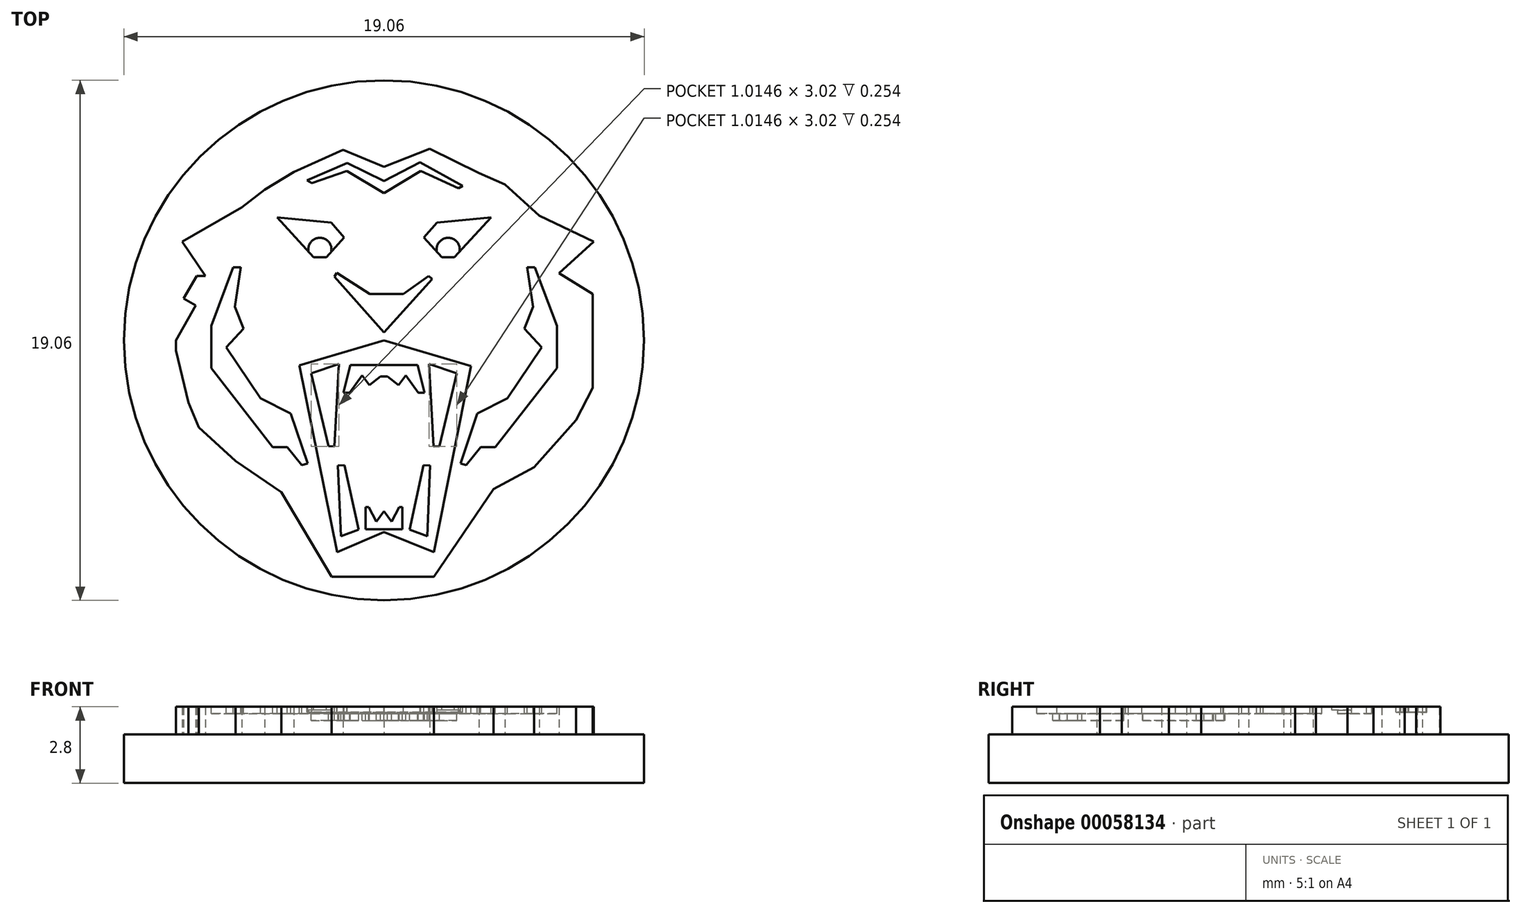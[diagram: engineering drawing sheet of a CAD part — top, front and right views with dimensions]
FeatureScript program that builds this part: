
annotation { "Feature Type Name" : "Feature", "Feature Type Description" : "" }
export const myFeature = defineFeature(function(context is Context, id is Id, definition is map)
    precondition{}
    {
        {
            var Q0;
            Q0=qCreatedBy(makeId("Top.planeOp"),FACE);
            var sketch = newSketch(context, id + "F0", { "sketchPlane" : qUnion([Q0])});
            skCircle(sketch, "E0", {"center": v(0, 0) * mm, "radius": 9.53 * mm});
            skSolve(sketch);
        }
        {
            var Q0;
            Q0=qCreatedBy(makeId("Top.planeOp"),FACE);
            var sketch = newSketch(context, id + "F1", { "sketchPlane" : qUnion([Q0])});
            skLineSegment(sketch, "E1", {"start": v(-7.39, 3.6) * mm, "end": v(-5.2, 4.87) * mm});
            skLineSegment(sketch, "E2", {"start": v(-5.2, 4.87) * mm, "end": v(-4.37, 5.52) * mm});
            skLineSegment(sketch, "E3", {"start": v(-4.37, 5.52) * mm, "end": v(-3.3, 6.17) * mm});
            skLineSegment(sketch, "E4", {"start": v(-3.3, 6.17) * mm, "end": v(-1.5, 6.98) * mm});
            skLineSegment(sketch, "E5", {"start": v(-1.5, 6.98) * mm, "end": v(0, 6.36) * mm});
            skLineSegment(sketch, "E6", {"start": v(0, 6.36) * mm, "end": v(1.67, 7.01) * mm});
            skLineSegment(sketch, "E7", {"start": v(1.67, 7.01) * mm, "end": v(3.47, 6.13) * mm});
            skLineSegment(sketch, "E8", {"start": v(3.47, 6.13) * mm, "end": v(4.43, 5.71) * mm});
            skLineSegment(sketch, "E9", {"start": v(4.43, 5.71) * mm, "end": v(5.69, 4.57) * mm});
            skLineSegment(sketch, "E10", {"start": v(5.69, 4.57) * mm, "end": v(7.68, 3.6) * mm});
            skLineSegment(sketch, "E11", {"start": v(7.68, 3.6) * mm, "end": v(6.42, 2.46) * mm});
            skLineSegment(sketch, "E12", {"start": v(6.42, 2.46) * mm, "end": v(7.64, 1.7) * mm});
            skLineSegment(sketch, "E13", {"start": v(7.64, 1.7) * mm, "end": v(7.64, 1.05) * mm});
            skLineSegment(sketch, "E14", {"start": v(7.64, 1.05) * mm, "end": v(7.64, 0.4) * mm});
            skLineSegment(sketch, "E15", {"start": v(7.64, 0.4) * mm, "end": v(7.64, -0.71) * mm});
            skLineSegment(sketch, "E16", {"start": v(7.64, -0.71) * mm, "end": v(7.64, -1.74) * mm});
            skLineSegment(sketch, "E17", {"start": v(7.64, -1.74) * mm, "end": v(7.03, -2.93) * mm});
            skLineSegment(sketch, "E18", {"start": v(7.03, -2.93) * mm, "end": v(5.5, -4.65) * mm});
            skLineSegment(sketch, "E19", {"start": v(5.5, -4.65) * mm, "end": v(4, -5.45) * mm});
            skLineSegment(sketch, "E20", {"start": v(4, -5.45) * mm, "end": v(1.83, -8.67) * mm});
            skLineSegment(sketch, "E21", {"start": v(1.83, -8.67) * mm, "end": v(-1.92, -8.67) * mm});
            skLineSegment(sketch, "E22", {"start": v(-1.92, -8.67) * mm, "end": v(-3.76, -5.57) * mm});
            skLineSegment(sketch, "E23", {"start": v(-3.76, -5.57) * mm, "end": v(-5.44, -4.42) * mm});
            skLineSegment(sketch, "E24", {"start": v(-5.44, -4.42) * mm, "end": v(-6.78, -3.2) * mm});
            skLineSegment(sketch, "E25", {"start": v(-6.78, -3.2) * mm, "end": v(-7.16, -2.28) * mm});
            skLineSegment(sketch, "E26", {"start": v(-7.16, -2.28) * mm, "end": v(-7.62, -0.37) * mm});
            skLineSegment(sketch, "E27", {"start": v(-7.62, -0.37) * mm, "end": v(-7.62, 0) * mm});
            skLineSegment(sketch, "E28", {"start": v(-7.62, 0) * mm, "end": v(-6.9, 1.28) * mm});
            skLineSegment(sketch, "E29", {"start": v(-6.9, 1.28) * mm, "end": v(-7.34, 1.53) * mm});
            skLineSegment(sketch, "E30", {"start": v(-7.34, 1.53) * mm, "end": v(-6.87, 2.36) * mm});
            skLineSegment(sketch, "E31", {"start": v(-6.87, 2.36) * mm, "end": v(-6.55, 2.36) * mm});
            skLineSegment(sketch, "E32", {"start": v(-6.55, 2.36) * mm, "end": v(-7.39, 3.6) * mm});
            skSolve(sketch);
        }
        {
            var Q0;
            Q0 = qSketchRegion(id + "F1", true);
            extrude(context, id + "F2", {"entities" : qUnion([Q0]), "depth" : 1.02 * mm});
        }
        {
            var Q0;
            Q0 = qSketchRegion(id + "F0", true);
            extrude(context, id + "F3", {"entities" : qUnion([Q0]), "operationType" : NewBodyOperationType.ADD, "oppositeDirection" : true, "depth" : 1.78 * mm});
        }
        {
            var Q0;
            Q0=makeQuery(id+"F2.opExtrude","CAP_FACE",FACE,{"disambiguationData":[OSD([sQuery(id+"F1.wireOp",EDGE,"E1"),sQuery(id+"F1.wireOp",EDGE,"E2"),sQuery(id+"F1.wireOp",EDGE,"E3"),sQuery(id+"F1.wireOp",EDGE,"E4"),sQuery(id+"F1.wireOp",EDGE,"E5"),sQuery(id+"F1.wireOp",EDGE,"E6"),sQuery(id+"F1.wireOp",EDGE,"E7"),sQuery(id+"F1.wireOp",EDGE,"E8"),sQuery(id+"F1.wireOp",EDGE,"E9"),sQuery(id+"F1.wireOp",EDGE,"E10"),sQuery(id+"F1.wireOp",EDGE,"E11"),sQuery(id+"F1.wireOp",EDGE,"E12"),sQuery(id+"F1.wireOp",EDGE,"E13"),sQuery(id+"F1.wireOp",EDGE,"E14"),sQuery(id+"F1.wireOp",EDGE,"E15"),sQuery(id+"F1.wireOp",EDGE,"E16"),sQuery(id+"F1.wireOp",EDGE,"E17"),sQuery(id+"F1.wireOp",EDGE,"E18"),sQuery(id+"F1.wireOp",EDGE,"E19"),sQuery(id+"F1.wireOp",EDGE,"E20"),sQuery(id+"F1.wireOp",EDGE,"E21"),sQuery(id+"F1.wireOp",EDGE,"E22"),sQuery(id+"F1.wireOp",EDGE,"E23"),sQuery(id+"F1.wireOp",EDGE,"E24"),sQuery(id+"F1.wireOp",EDGE,"E25"),sQuery(id+"F1.wireOp",EDGE,"E26"),sQuery(id+"F1.wireOp",EDGE,"E27"),sQuery(id+"F1.wireOp",EDGE,"E28"),sQuery(id+"F1.wireOp",EDGE,"E29"),sQuery(id+"F1.wireOp",EDGE,"E30"),sQuery(id+"F1.wireOp",EDGE,"E31"),sQuery(id+"F1.wireOp",EDGE,"E32")])],"isStart":false});
            var sketch = newSketch(context, id + "F4", { "sketchPlane" : qUnion([Q0])});
            skLineSegment(sketch, "E33", {"start": v(15.35, 3.18) * mm, "end": v(17.71, 4.55) * mm});
            skLineSegment(sketch, "E34", {"start": v(17.71, 4.55) * mm, "end": v(18.63, 5.25) * mm});
            skLineSegment(sketch, "E35", {"start": v(18.63, 5.25) * mm, "end": v(19.79, 5.96) * mm});
            skLineSegment(sketch, "E36", {"start": v(19.79, 5.96) * mm, "end": v(21.74, 6.83) * mm});
            skLineSegment(sketch, "E37", {"start": v(21.74, 6.83) * mm, "end": v(23.36, 6.16) * mm});
            skLineSegment(sketch, "E38", {"start": v(23.36, 6.16) * mm, "end": v(25.18, 6.87) * mm});
            skLineSegment(sketch, "E39", {"start": v(25.18, 6.87) * mm, "end": v(27.13, 5.91) * mm});
            skLineSegment(sketch, "E40", {"start": v(27.13, 5.91) * mm, "end": v(28.16, 5.46) * mm});
            skLineSegment(sketch, "E41", {"start": v(28.16, 5.46) * mm, "end": v(29.53, 4.21) * mm});
            skLineSegment(sketch, "E42", {"start": v(29.53, 4.21) * mm, "end": v(31.69, 3.18) * mm});
            skLineSegment(sketch, "E43", {"start": v(31.69, 3.18) * mm, "end": v(30.32, 1.93) * mm});
            skLineSegment(sketch, "E44", {"start": v(30.32, 1.93) * mm, "end": v(31.65, 1.1) * mm});
            skLineSegment(sketch, "E45", {"start": v(31.65, 1.1) * mm, "end": v(31.65, 0.4) * mm});
            skLineSegment(sketch, "E46", {"start": v(31.65, 0.4) * mm, "end": v(31.65, -0.3) * mm});
            skLineSegment(sketch, "E47", {"start": v(31.65, -0.3) * mm, "end": v(31.65, -1.5) * mm});
            skLineSegment(sketch, "E48", {"start": v(31.65, -1.5) * mm, "end": v(31.65, -2.63) * mm});
            skLineSegment(sketch, "E49", {"start": v(31.65, -2.63) * mm, "end": v(30.98, -3.91) * mm});
            skLineSegment(sketch, "E50", {"start": v(30.98, -3.91) * mm, "end": v(29.32, -5.78) * mm});
            skLineSegment(sketch, "E51", {"start": v(29.32, -5.78) * mm, "end": v(27.7, -6.65) * mm});
            skLineSegment(sketch, "E52", {"start": v(27.7, -6.65) * mm, "end": v(25.34, -10.13) * mm});
            skLineSegment(sketch, "E53", {"start": v(25.34, -10.13) * mm, "end": v(21.28, -10.13) * mm});
            skLineSegment(sketch, "E54", {"start": v(21.28, -10.13) * mm, "end": v(19.29, -6.77) * mm});
            skLineSegment(sketch, "E55", {"start": v(19.29, -6.77) * mm, "end": v(17.46, -5.53) * mm});
            skLineSegment(sketch, "E56", {"start": v(17.46, -5.53) * mm, "end": v(16.01, -4.2) * mm});
            skLineSegment(sketch, "E57", {"start": v(16.01, -4.2) * mm, "end": v(15.6, -3.2) * mm});
            skLineSegment(sketch, "E58", {"start": v(15.6, -3.2) * mm, "end": v(15.1, -1.13) * mm});
            skLineSegment(sketch, "E59", {"start": v(15.1, -1.13) * mm, "end": v(15.1, -0.74) * mm});
            skLineSegment(sketch, "E60", {"start": v(15.1, -0.74) * mm, "end": v(15.89, 0.65) * mm});
            skLineSegment(sketch, "E61", {"start": v(15.89, 0.65) * mm, "end": v(15.4, 0.92) * mm});
            skLineSegment(sketch, "E62", {"start": v(15.4, 0.92) * mm, "end": v(15.92, 1.82) * mm});
            skLineSegment(sketch, "E63", {"start": v(15.92, 1.82) * mm, "end": v(16.26, 1.82) * mm});
            skLineSegment(sketch, "E64", {"start": v(16.26, 1.82) * mm, "end": v(15.35, 3.18) * mm});
            skLineSegment(sketch, "E65", {"start": v(18.44, 1.72) * mm, "end": v(19.91, 2.58) * mm});
            skLineSegment(sketch, "E66", {"start": v(19.91, 2.58) * mm, "end": v(20.48, 3.02) * mm});
            skLineSegment(sketch, "E67", {"start": v(20.48, 3.02) * mm, "end": v(21.2, 3.46) * mm});
            skLineSegment(sketch, "E68", {"start": v(21.2, 3.46) * mm, "end": v(22.43, 4) * mm});
            skLineSegment(sketch, "E69", {"start": v(22.43, 4) * mm, "end": v(23.44, 3.59) * mm});
            skLineSegment(sketch, "E70", {"start": v(23.44, 3.59) * mm, "end": v(24.58, 4.03) * mm});
            skLineSegment(sketch, "E71", {"start": v(24.58, 4.03) * mm, "end": v(25.8, 3.43) * mm});
            skLineSegment(sketch, "E72", {"start": v(25.8, 3.43) * mm, "end": v(26.44, 3.15) * mm});
            skLineSegment(sketch, "E73", {"start": v(26.44, 3.15) * mm, "end": v(27.3, 2.37) * mm});
            skLineSegment(sketch, "E74", {"start": v(27.3, 2.37) * mm, "end": v(28.65, 1.72) * mm});
            skLineSegment(sketch, "E75", {"start": v(28.65, 1.72) * mm, "end": v(27.8, 0.94) * mm});
            skLineSegment(sketch, "E76", {"start": v(27.8, 0.94) * mm, "end": v(28.62, 0.43) * mm});
            skLineSegment(sketch, "E77", {"start": v(28.62, 0.43) * mm, "end": v(28.62, -0.66) * mm});
            skLineSegment(sketch, "E78", {"start": v(28.62, -0.66) * mm, "end": v(28.62, -1.1) * mm});
            skLineSegment(sketch, "E79", {"start": v(28.62, -1.1) * mm, "end": v(28.62, -1.86) * mm});
            skLineSegment(sketch, "E80", {"start": v(28.62, -1.86) * mm, "end": v(28.62, -1.9) * mm});
            skLineSegment(sketch, "E81", {"start": v(28.62, -1.9) * mm, "end": v(28.2, -2.71) * mm});
            skLineSegment(sketch, "E82", {"start": v(28.2, -2.71) * mm, "end": v(27.17, -3.88) * mm});
            skLineSegment(sketch, "E83", {"start": v(27.17, -3.88) * mm, "end": v(26.16, -4.42) * mm});
            skLineSegment(sketch, "E84", {"start": v(26.16, -4.42) * mm, "end": v(24.68, -6.6) * mm});
            skLineSegment(sketch, "E85", {"start": v(24.68, -6.6) * mm, "end": v(22.14, -6.6) * mm});
            skLineSegment(sketch, "E86", {"start": v(22.14, -6.6) * mm, "end": v(20.9, -4.5) * mm});
            skLineSegment(sketch, "E87", {"start": v(20.9, -4.5) * mm, "end": v(19.76, -3.72) * mm});
            skLineSegment(sketch, "E88", {"start": v(19.76, -3.72) * mm, "end": v(18.85, -2.9) * mm});
            skLineSegment(sketch, "E89", {"start": v(18.85, -2.9) * mm, "end": v(18.6, -2.27) * mm});
            skLineSegment(sketch, "E90", {"start": v(18.6, -2.27) * mm, "end": v(18.28, -0.97) * mm});
            skLineSegment(sketch, "E91", {"start": v(18.28, -0.97) * mm, "end": v(18.28, -0.72) * mm});
            skLineSegment(sketch, "E92", {"start": v(18.28, -0.72) * mm, "end": v(18.77, 0.14) * mm});
            skLineSegment(sketch, "E93", {"start": v(18.77, 0.14) * mm, "end": v(18.47, 0.31) * mm});
            skLineSegment(sketch, "E94", {"start": v(18.47, 0.31) * mm, "end": v(18.8, 0.87) * mm});
            skLineSegment(sketch, "E95", {"start": v(18.8, 0.87) * mm, "end": v(19, 0.87) * mm});
            skLineSegment(sketch, "E96", {"start": v(19, 0.87) * mm, "end": v(18.44, 1.72) * mm});
            skLineSegment(sketch, "E97", {"start": v(18.44, 1.71) * mm, "end": v(19.91, 2.57) * mm});
            skLineSegment(sketch, "E98", {"start": v(19.91, 2.57) * mm, "end": v(20.48, 3.01) * mm});
            skLineSegment(sketch, "E99", {"start": v(20.48, 3.01) * mm, "end": v(21.2, 3.45) * mm});
            skLineSegment(sketch, "E100", {"start": v(21.2, 3.45) * mm, "end": v(22.43, 4) * mm});
            skLineSegment(sketch, "E101", {"start": v(22.43, 4) * mm, "end": v(23.44, 3.58) * mm});
            skLineSegment(sketch, "E102", {"start": v(23.44, 3.58) * mm, "end": v(25.3, 4.85) * mm});
            skLineSegment(sketch, "E103", {"start": v(25.3, 4.85) * mm, "end": v(25.8, 3.43) * mm});
            skLineSegment(sketch, "E104", {"start": v(25.8, 3.43) * mm, "end": v(26.44, 3.14) * mm});
            skLineSegment(sketch, "E105", {"start": v(26.44, 3.14) * mm, "end": v(27.3, 2.36) * mm});
            skLineSegment(sketch, "E106", {"start": v(27.3, 2.36) * mm, "end": v(28.65, 1.71) * mm});
            skLineSegment(sketch, "E107", {"start": v(28.65, 1.71) * mm, "end": v(27.8, 0.94) * mm});
            skLineSegment(sketch, "E108", {"start": v(27.8, 0.94) * mm, "end": v(28.62, 0.42) * mm});
            skLineSegment(sketch, "E109", {"start": v(28.62, 0.42) * mm, "end": v(28.62, -0.6) * mm});
            skLineSegment(sketch, "E110", {"start": v(28.62, -0.6) * mm, "end": v(28.62, -1.04) * mm});
            skLineSegment(sketch, "E111", {"start": v(28.62, -1.04) * mm, "end": v(28.62, -1.79) * mm});
            skLineSegment(sketch, "E112", {"start": v(28.62, -1.79) * mm, "end": v(28.62, -1.91) * mm});
            skLineSegment(sketch, "E113", {"start": v(28.62, -1.91) * mm, "end": v(28.2, -2.72) * mm});
            skLineSegment(sketch, "E114", {"start": v(28.2, -2.72) * mm, "end": v(27.17, -3.88) * mm});
            skLineSegment(sketch, "E115", {"start": v(27.17, -3.88) * mm, "end": v(26.16, -4.43) * mm});
            skLineSegment(sketch, "E116", {"start": v(26.16, -4.43) * mm, "end": v(24.68, -6.6) * mm});
            skLineSegment(sketch, "E117", {"start": v(20.9, -4.5) * mm, "end": v(19.76, -3.73) * mm});
            skLineSegment(sketch, "E118", {"start": v(19.76, -3.73) * mm, "end": v(18.85, -2.9) * mm});
            skLineSegment(sketch, "E119", {"start": v(18.85, -2.9) * mm, "end": v(18.6, -2.28) * mm});
            skLineSegment(sketch, "E120", {"start": v(18.6, -2.28) * mm, "end": v(18.28, -0.98) * mm});
            skLineSegment(sketch, "E121", {"start": v(18.28, -0.98) * mm, "end": v(18.28, -0.73) * mm});
            skLineSegment(sketch, "E122", {"start": v(18.28, -0.73) * mm, "end": v(18.77, 0.13) * mm});
            skLineSegment(sketch, "E123", {"start": v(18.77, 0.13) * mm, "end": v(18.47, 0.3) * mm});
            skLineSegment(sketch, "E124", {"start": v(18.47, 0.3) * mm, "end": v(18.8, 0.87) * mm});
            skLineSegment(sketch, "E125", {"start": v(19, 0.87) * mm, "end": v(18.44, 1.71) * mm});
            skSolve(sketch);
        }
        {
            var Q0;
            Q0=makeQuery(id+"F4.imprint","IMPRINT",FACE,{"disambiguationData":[TD([[makeQuery(id+"F4.imprint","IMPRINT",EDGE,{"derivedFrom":sQuery(id+"F4.wireOp",EDGE,"E33")}),-1.0]])]});
            extrude(context, id + "F5", {"entities" : qUnion([Q0]), "depth" : 0.74 * mm});
        }
        {
            var Q0;
            Q0=makeQuery(id+"F5.opExtrude","SWEPT_BODY",BODY,{"disambiguationData":[OSD([sQuery(id+"F4.wireOp",EDGE,"E33"),sQuery(id+"F4.wireOp",EDGE,"E34"),sQuery(id+"F4.wireOp",EDGE,"E35"),sQuery(id+"F4.wireOp",EDGE,"E36"),sQuery(id+"F4.wireOp",EDGE,"E37"),sQuery(id+"F4.wireOp",EDGE,"E38"),sQuery(id+"F4.wireOp",EDGE,"E39"),sQuery(id+"F4.wireOp",EDGE,"E40"),sQuery(id+"F4.wireOp",EDGE,"E41"),sQuery(id+"F4.wireOp",EDGE,"E42"),sQuery(id+"F4.wireOp",EDGE,"E43"),sQuery(id+"F4.wireOp",EDGE,"E44"),sQuery(id+"F4.wireOp",EDGE,"E45"),sQuery(id+"F4.wireOp",EDGE,"E46"),sQuery(id+"F4.wireOp",EDGE,"E47"),sQuery(id+"F4.wireOp",EDGE,"E48"),sQuery(id+"F4.wireOp",EDGE,"E49"),sQuery(id+"F4.wireOp",EDGE,"E50"),sQuery(id+"F4.wireOp",EDGE,"E51"),sQuery(id+"F4.wireOp",EDGE,"E52"),sQuery(id+"F4.wireOp",EDGE,"E53"),sQuery(id+"F4.wireOp",EDGE,"E54"),sQuery(id+"F4.wireOp",EDGE,"E55"),sQuery(id+"F4.wireOp",EDGE,"E56"),sQuery(id+"F4.wireOp",EDGE,"E57"),sQuery(id+"F4.wireOp",EDGE,"E58"),sQuery(id+"F4.wireOp",EDGE,"E59"),sQuery(id+"F4.wireOp",EDGE,"E60"),sQuery(id+"F4.wireOp",EDGE,"E61"),sQuery(id+"F4.wireOp",EDGE,"E62"),sQuery(id+"F4.wireOp",EDGE,"E63"),sQuery(id+"F4.wireOp",EDGE,"E64"),sQuery(id+"F4.wireOp",EDGE,"E65"),sQuery(id+"F4.wireOp",EDGE,"E66"),sQuery(id+"F4.wireOp",EDGE,"E67"),sQuery(id+"F4.wireOp",EDGE,"E68"),sQuery(id+"F4.wireOp",EDGE,"E69"),sQuery(id+"F4.wireOp",EDGE,"E70"),sQuery(id+"F4.wireOp",EDGE,"E71"),sQuery(id+"F4.wireOp",EDGE,"E72"),sQuery(id+"F4.wireOp",EDGE,"E73"),sQuery(id+"F4.wireOp",EDGE,"E74"),sQuery(id+"F4.wireOp",EDGE,"E75"),sQuery(id+"F4.wireOp",EDGE,"E76"),sQuery(id+"F4.wireOp",EDGE,"E77"),sQuery(id+"F4.wireOp",EDGE,"E91"),sQuery(id+"F4.wireOp",EDGE,"E92"),sQuery(id+"F4.wireOp",EDGE,"E93"),sQuery(id+"F4.wireOp",EDGE,"E94"),sQuery(id+"F4.wireOp",EDGE,"E95"),sQuery(id+"F4.wireOp",EDGE,"E96"),sQuery(id+"F4.wireOp",EDGE,"E97"),sQuery(id+"F4.wireOp",EDGE,"E102"),sQuery(id+"F4.wireOp",EDGE,"E103"),sQuery(id+"F4.wireOp",EDGE,"E106"),sQuery(id+"F4.wireOp",EDGE,"E107"),sQuery(id+"F4.wireOp",EDGE,"E109"),sQuery(id+"F4.wireOp",EDGE,"E110"),sQuery(id+"F4.wireOp",EDGE,"E111"),sQuery(id+"F4.wireOp",EDGE,"E112"),sQuery(id+"F4.wireOp",EDGE,"E113"),sQuery(id+"F4.wireOp",EDGE,"E114"),sQuery(id+"F4.wireOp",EDGE,"E115"),sQuery(id+"F4.wireOp",EDGE,"E116"),sQuery(id+"F4.wireOp",EDGE,"E85"),sQuery(id+"F4.wireOp",EDGE,"E86"),sQuery(id+"F4.wireOp",EDGE,"E117"),sQuery(id+"F4.wireOp",EDGE,"E118"),sQuery(id+"F4.wireOp",EDGE,"E119"),sQuery(id+"F4.wireOp",EDGE,"E120"),sQuery(id+"F4.wireOp",EDGE,"E121"),sQuery(id+"F4.wireOp",EDGE,"E123"),sQuery(id+"F4.wireOp",EDGE,"E124"),sQuery(id+"F4.wireOp",EDGE,"E125")])]});
            deleteBodies(context, id + "F6", {"entities" : qUnion([Q0])});
        }
        {
            var Q0;
            Q0=makeQuery(id+"F2.opExtrude","CAP_FACE",FACE,{"disambiguationData":[OSD([sQuery(id+"F1.wireOp",EDGE,"E1"),sQuery(id+"F1.wireOp",EDGE,"E2"),sQuery(id+"F1.wireOp",EDGE,"E3"),sQuery(id+"F1.wireOp",EDGE,"E4"),sQuery(id+"F1.wireOp",EDGE,"E5"),sQuery(id+"F1.wireOp",EDGE,"E6"),sQuery(id+"F1.wireOp",EDGE,"E7"),sQuery(id+"F1.wireOp",EDGE,"E8"),sQuery(id+"F1.wireOp",EDGE,"E9"),sQuery(id+"F1.wireOp",EDGE,"E10"),sQuery(id+"F1.wireOp",EDGE,"E11"),sQuery(id+"F1.wireOp",EDGE,"E12"),sQuery(id+"F1.wireOp",EDGE,"E13"),sQuery(id+"F1.wireOp",EDGE,"E14"),sQuery(id+"F1.wireOp",EDGE,"E15"),sQuery(id+"F1.wireOp",EDGE,"E16"),sQuery(id+"F1.wireOp",EDGE,"E17"),sQuery(id+"F1.wireOp",EDGE,"E18"),sQuery(id+"F1.wireOp",EDGE,"E19"),sQuery(id+"F1.wireOp",EDGE,"E20"),sQuery(id+"F1.wireOp",EDGE,"E21"),sQuery(id+"F1.wireOp",EDGE,"E22"),sQuery(id+"F1.wireOp",EDGE,"E23"),sQuery(id+"F1.wireOp",EDGE,"E24"),sQuery(id+"F1.wireOp",EDGE,"E25"),sQuery(id+"F1.wireOp",EDGE,"E26"),sQuery(id+"F1.wireOp",EDGE,"E27"),sQuery(id+"F1.wireOp",EDGE,"E28"),sQuery(id+"F1.wireOp",EDGE,"E29"),sQuery(id+"F1.wireOp",EDGE,"E30"),sQuery(id+"F1.wireOp",EDGE,"E31"),sQuery(id+"F1.wireOp",EDGE,"E32")])],"isStart":false});
            var sketch = newSketch(context, id + "F7", { "sketchPlane" : qUnion([Q0])});
            skLineSegment(sketch, "E126", {"start": v(-2.82, 5.86) * mm, "end": v(-1.35, 6.5) * mm});
            skLineSegment(sketch, "E127", {"start": v(-1.35, 6.5) * mm, "end": v(0, 5.84) * mm});
            skLineSegment(sketch, "E128", {"start": v(0, 5.84) * mm, "end": v(1.32, 6.52) * mm});
            skLineSegment(sketch, "E129", {"start": v(1.32, 6.52) * mm, "end": v(2.88, 5.67) * mm});
            skLineSegment(sketch, "E130", {"start": v(2.88, 5.67) * mm, "end": v(2.73, 5.57) * mm});
            skLineSegment(sketch, "E131", {"start": v(2.73, 5.57) * mm, "end": v(1.34, 6.2) * mm});
            skLineSegment(sketch, "E132", {"start": v(1.34, 6.2) * mm, "end": v(0, 5.39) * mm});
            skLineSegment(sketch, "E133", {"start": v(0, 5.39) * mm, "end": v(-1.36, 6.2) * mm});
            skLineSegment(sketch, "E134", {"start": v(-1.36, 6.2) * mm, "end": v(-2.64, 5.76) * mm});
            skLineSegment(sketch, "E135", {"start": v(-2.64, 5.76) * mm, "end": v(-2.82, 5.86) * mm});
            skSolve(sketch);
        }
        {
            var Q0;
            Q0 = qSketchRegion(id + "F7", true);
            extrude(context, id + "F8", {"entities" : qUnion([Q0]), "operationType" : NewBodyOperationType.REMOVE, "oppositeDirection" : true, "depth" : 0.2 * mm});
        }
        {
            var Q0;
            Q0=makeQuery(id+"F2.opExtrude","CAP_FACE",FACE,{"disambiguationData":[OSD([sQuery(id+"F1.wireOp",EDGE,"E1"),sQuery(id+"F1.wireOp",EDGE,"E2"),sQuery(id+"F1.wireOp",EDGE,"E3"),sQuery(id+"F1.wireOp",EDGE,"E4"),sQuery(id+"F1.wireOp",EDGE,"E5"),sQuery(id+"F1.wireOp",EDGE,"E6"),sQuery(id+"F1.wireOp",EDGE,"E7"),sQuery(id+"F1.wireOp",EDGE,"E8"),sQuery(id+"F1.wireOp",EDGE,"E9"),sQuery(id+"F1.wireOp",EDGE,"E10"),sQuery(id+"F1.wireOp",EDGE,"E11"),sQuery(id+"F1.wireOp",EDGE,"E12"),sQuery(id+"F1.wireOp",EDGE,"E13"),sQuery(id+"F1.wireOp",EDGE,"E14"),sQuery(id+"F1.wireOp",EDGE,"E15"),sQuery(id+"F1.wireOp",EDGE,"E16"),sQuery(id+"F1.wireOp",EDGE,"E17"),sQuery(id+"F1.wireOp",EDGE,"E18"),sQuery(id+"F1.wireOp",EDGE,"E19"),sQuery(id+"F1.wireOp",EDGE,"E20"),sQuery(id+"F1.wireOp",EDGE,"E21"),sQuery(id+"F1.wireOp",EDGE,"E22"),sQuery(id+"F1.wireOp",EDGE,"E23"),sQuery(id+"F1.wireOp",EDGE,"E24"),sQuery(id+"F1.wireOp",EDGE,"E25"),sQuery(id+"F1.wireOp",EDGE,"E26"),sQuery(id+"F1.wireOp",EDGE,"E27"),sQuery(id+"F1.wireOp",EDGE,"E28"),sQuery(id+"F1.wireOp",EDGE,"E29"),sQuery(id+"F1.wireOp",EDGE,"E30"),sQuery(id+"F1.wireOp",EDGE,"E31"),sQuery(id+"F1.wireOp",EDGE,"E32")])],"isStart":false});
            var sketch = newSketch(context, id + "F9", { "sketchPlane" : qUnion([Q0])});
            skLineSegment(sketch, "E136", {"start": v(-2.8, -4.5) * mm, "end": v(-3.42, -2.68) * mm});
            skLineSegment(sketch, "E137", {"start": v(-3.42, -2.68) * mm, "end": v(-4.52, -2.13) * mm});
            skLineSegment(sketch, "E138", {"start": v(-4.52, -2.13) * mm, "end": v(-5.78, -0.26) * mm});
            skLineSegment(sketch, "E139", {"start": v(-5.78, -0.26) * mm, "end": v(-5.14, 0.43) * mm});
            skLineSegment(sketch, "E140", {"start": v(-5.14, 0.43) * mm, "end": v(-5.46, 1.23) * mm});
            skLineSegment(sketch, "E141", {"start": v(-5.46, 1.23) * mm, "end": v(-5.25, 2.68) * mm});
            skLineSegment(sketch, "E142", {"start": v(-5.25, 2.68) * mm, "end": v(-5.52, 2.68) * mm});
            skLineSegment(sketch, "E143", {"start": v(-5.52, 2.68) * mm, "end": v(-6.33, 0.53) * mm});
            skLineSegment(sketch, "E144", {"start": v(-6.33, 0.53) * mm, "end": v(-6.33, -1.02) * mm});
            skLineSegment(sketch, "E145", {"start": v(-6.33, -1.02) * mm, "end": v(-4.08, -3.91) * mm});
            skLineSegment(sketch, "E146", {"start": v(-4.08, -3.91) * mm, "end": v(-3.55, -3.91) * mm});
            skLineSegment(sketch, "E147", {"start": v(-3.55, -3.91) * mm, "end": v(-3.01, -4.57) * mm});
            skLineSegment(sketch, "E148", {"start": v(-3.01, -4.57) * mm, "end": v(-2.8, -4.5) * mm});
            skLineSegment(sketch, "E149.MirrorCS", {"start": v(5.25, 2.68) * mm, "end": v(5.52, 2.68) * mm});
            skLineSegment(sketch, "E150.MirrorCS", {"start": v(4.08, -3.91) * mm, "end": v(3.55, -3.91) * mm});
            skLineSegment(sketch, "E151.MirrorCS", {"start": v(3.01, -4.57) * mm, "end": v(2.8, -4.5) * mm});
            skLineSegment(sketch, "E152.MirrorCS", {"start": v(2.8, -4.5) * mm, "end": v(3.42, -2.68) * mm});
            skLineSegment(sketch, "E153.MirrorCS", {"start": v(3.42, -2.68) * mm, "end": v(4.52, -2.13) * mm});
            skLineSegment(sketch, "E154.MirrorCS", {"start": v(4.52, -2.13) * mm, "end": v(5.78, -0.26) * mm});
            skLineSegment(sketch, "E155.MirrorCS", {"start": v(5.78, -0.26) * mm, "end": v(5.14, 0.43) * mm});
            skLineSegment(sketch, "E156.MirrorCS", {"start": v(5.14, 0.43) * mm, "end": v(5.46, 1.23) * mm});
            skLineSegment(sketch, "E157.MirrorCS", {"start": v(5.46, 1.23) * mm, "end": v(5.25, 2.68) * mm});
            skLineSegment(sketch, "E158.MirrorCS", {"start": v(5.52, 2.68) * mm, "end": v(6.33, 0.53) * mm});
            skLineSegment(sketch, "E159.MirrorCS", {"start": v(6.33, 0.53) * mm, "end": v(6.33, -1.02) * mm});
            skLineSegment(sketch, "E160.MirrorCS", {"start": v(3.55, -3.91) * mm, "end": v(3.01, -4.57) * mm});
            skLineSegment(sketch, "E161.MirrorCS", {"start": v(6.33, -1.02) * mm, "end": v(4.08, -3.91) * mm});
            skSolve(sketch);
        }
        {
            var Q0;
            Q0 = qSketchRegion(id + "F9", true);
            extrude(context, id + "F10", {"entities" : qUnion([Q0]), "operationType" : NewBodyOperationType.REMOVE, "oppositeDirection" : true, "depth" : 0.25 * mm});
        }
        {
            var Q0;
            Q0=makeQuery(id+"F2.opExtrude","CAP_FACE",FACE,{"disambiguationData":[OSD([sQuery(id+"F1.wireOp",EDGE,"E1"),sQuery(id+"F1.wireOp",EDGE,"E2"),sQuery(id+"F1.wireOp",EDGE,"E3"),sQuery(id+"F1.wireOp",EDGE,"E4"),sQuery(id+"F1.wireOp",EDGE,"E5"),sQuery(id+"F1.wireOp",EDGE,"E6"),sQuery(id+"F1.wireOp",EDGE,"E7"),sQuery(id+"F1.wireOp",EDGE,"E8"),sQuery(id+"F1.wireOp",EDGE,"E9"),sQuery(id+"F1.wireOp",EDGE,"E10"),sQuery(id+"F1.wireOp",EDGE,"E11"),sQuery(id+"F1.wireOp",EDGE,"E12"),sQuery(id+"F1.wireOp",EDGE,"E13"),sQuery(id+"F1.wireOp",EDGE,"E14"),sQuery(id+"F1.wireOp",EDGE,"E15"),sQuery(id+"F1.wireOp",EDGE,"E16"),sQuery(id+"F1.wireOp",EDGE,"E17"),sQuery(id+"F1.wireOp",EDGE,"E18"),sQuery(id+"F1.wireOp",EDGE,"E19"),sQuery(id+"F1.wireOp",EDGE,"E20"),sQuery(id+"F1.wireOp",EDGE,"E21"),sQuery(id+"F1.wireOp",EDGE,"E22"),sQuery(id+"F1.wireOp",EDGE,"E23"),sQuery(id+"F1.wireOp",EDGE,"E24"),sQuery(id+"F1.wireOp",EDGE,"E25"),sQuery(id+"F1.wireOp",EDGE,"E26"),sQuery(id+"F1.wireOp",EDGE,"E27"),sQuery(id+"F1.wireOp",EDGE,"E28"),sQuery(id+"F1.wireOp",EDGE,"E29"),sQuery(id+"F1.wireOp",EDGE,"E30"),sQuery(id+"F1.wireOp",EDGE,"E31"),sQuery(id+"F1.wireOp",EDGE,"E32")])],"isStart":false});
            var sketch = newSketch(context, id + "F11", { "sketchPlane" : qUnion([Q0])});
            skLineSegment(sketch, "E162", {"start": v(-3.1, -0.92) * mm, "end": v(0, 0) * mm});
            skLineSegment(sketch, "E163", {"start": v(0, 0) * mm, "end": v(3.18, -0.94) * mm});
            skLineSegment(sketch, "E164", {"start": v(3.18, -0.94) * mm, "end": v(1.82, -7.77) * mm});
            skLineSegment(sketch, "E165", {"start": v(1.82, -7.77) * mm, "end": v(0, -7.03) * mm});
            skLineSegment(sketch, "E166", {"start": v(0, -7.03) * mm, "end": v(-1.71, -7.77) * mm});
            skLineSegment(sketch, "E167", {"start": v(-1.71, -7.77) * mm, "end": v(-3.1, -0.92) * mm});
            skSolve(sketch);
        }
        {
            var Q0;
            Q0 = qSketchRegion(id + "F11", true);
            extrude(context, id + "F12", {"entities" : qUnion([Q0]), "operationType" : NewBodyOperationType.REMOVE, "oppositeDirection" : true, "depth" : 0.25 * mm});
        }
        {
            var Q0;
            Q0=makeQuery(id+"F2.opExtrude","CAP_FACE",FACE,{"disambiguationData":[OSD([sQuery(id+"F1.wireOp",EDGE,"E1"),sQuery(id+"F1.wireOp",EDGE,"E2"),sQuery(id+"F1.wireOp",EDGE,"E3"),sQuery(id+"F1.wireOp",EDGE,"E4"),sQuery(id+"F1.wireOp",EDGE,"E5"),sQuery(id+"F1.wireOp",EDGE,"E6"),sQuery(id+"F1.wireOp",EDGE,"E7"),sQuery(id+"F1.wireOp",EDGE,"E8"),sQuery(id+"F1.wireOp",EDGE,"E9"),sQuery(id+"F1.wireOp",EDGE,"E10"),sQuery(id+"F1.wireOp",EDGE,"E11"),sQuery(id+"F1.wireOp",EDGE,"E12"),sQuery(id+"F1.wireOp",EDGE,"E13"),sQuery(id+"F1.wireOp",EDGE,"E14"),sQuery(id+"F1.wireOp",EDGE,"E15"),sQuery(id+"F1.wireOp",EDGE,"E16"),sQuery(id+"F1.wireOp",EDGE,"E17"),sQuery(id+"F1.wireOp",EDGE,"E18"),sQuery(id+"F1.wireOp",EDGE,"E19"),sQuery(id+"F1.wireOp",EDGE,"E20"),sQuery(id+"F1.wireOp",EDGE,"E21"),sQuery(id+"F1.wireOp",EDGE,"E22"),sQuery(id+"F1.wireOp",EDGE,"E23"),sQuery(id+"F1.wireOp",EDGE,"E24"),sQuery(id+"F1.wireOp",EDGE,"E25"),sQuery(id+"F1.wireOp",EDGE,"E26"),sQuery(id+"F1.wireOp",EDGE,"E27"),sQuery(id+"F1.wireOp",EDGE,"E28"),sQuery(id+"F1.wireOp",EDGE,"E29"),sQuery(id+"F1.wireOp",EDGE,"E30"),sQuery(id+"F1.wireOp",EDGE,"E31"),sQuery(id+"F1.wireOp",EDGE,"E32")])],"isStart":false});
            var sketch = newSketch(context, id + "F13", { "sketchPlane" : qUnion([Q0])});
            skLineSegment(sketch, "E168", {"start": v(0, 0.29) * mm, "end": v(1.76, 2.24) * mm});
            skLineSegment(sketch, "E169", {"start": v(1.76, 2.24) * mm, "end": v(1.64, 2.36) * mm});
            skLineSegment(sketch, "E170", {"start": v(1.64, 2.36) * mm, "end": v(0.71, 1.7) * mm});
            skLineSegment(sketch, "E171", {"start": v(0.71, 1.7) * mm, "end": v(-0.53, 1.7) * mm});
            skLineSegment(sketch, "E172", {"start": v(-0.53, 1.7) * mm, "end": v(-1.73, 2.47) * mm});
            skLineSegment(sketch, "E173", {"start": v(-1.73, 2.47) * mm, "end": v(-1.82, 2.33) * mm});
            skLineSegment(sketch, "E174", {"start": v(-1.82, 2.33) * mm, "end": v(0, 0.29) * mm});
            skLineSegment(sketch, "E175", {"start": v(-1.46, 3.77) * mm, "end": v(-1.94, 4.3) * mm});
            skLineSegment(sketch, "E176", {"start": v(-1.94, 4.3) * mm, "end": v(-3.92, 4.5) * mm});
            skLineSegment(sketch, "E177", {"start": v(-3.92, 4.5) * mm, "end": v(-2.58, 3.04) * mm});
            skLineSegment(sketch, "E178", {"start": v(-2.58, 3.04) * mm, "end": v(-2.12, 3.04) * mm});
            skLineSegment(sketch, "E179", {"start": v(-2.12, 3.04) * mm, "end": v(-1.46, 3.77) * mm});
            skLineSegment(sketch, "E180.MirrorCS", {"start": v(2.12, 3.04) * mm, "end": v(1.46, 3.77) * mm});
            skLineSegment(sketch, "E181.MirrorCS", {"start": v(2.58, 3.04) * mm, "end": v(2.12, 3.04) * mm});
            skLineSegment(sketch, "E182.MirrorCS", {"start": v(3.92, 4.5) * mm, "end": v(2.58, 3.04) * mm});
            skLineSegment(sketch, "E183.MirrorCS", {"start": v(1.46, 3.77) * mm, "end": v(1.94, 4.3) * mm});
            skLineSegment(sketch, "E184.MirrorCS", {"start": v(1.94, 4.3) * mm, "end": v(3.92, 4.5) * mm});
            skSolve(sketch);
        }
        {
            var Q0;
            Q0 = qSketchRegion(id + "F13", true);
            extrude(context, id + "F14", {"entities" : qUnion([Q0]), "operationType" : NewBodyOperationType.REMOVE, "oppositeDirection" : true, "depth" : 0.25 * mm});
        }
        {
            var Q0;
            Q0=makeQuery(id+"F14.boolean.opBoolean","COPY",FACE,{"derivedFrom":makeQuery(id+"F14.opExtrude","CAP_FACE",FACE,{"disambiguationData":[OSD([sQuery(id+"F13.wireOp",EDGE,"E183.MirrorCS"),sQuery(id+"F13.wireOp",EDGE,"E184.MirrorCS"),sQuery(id+"F13.wireOp",EDGE,"E182.MirrorCS"),sQuery(id+"F13.wireOp",EDGE,"E181.MirrorCS"),sQuery(id+"F13.wireOp",EDGE,"E180.MirrorCS")])],"isStart":false})});
            var sketch = newSketch(context, id + "F15", { "sketchPlane" : qUnion([Q0])});
            skArc(sketch, "E185", {"start": v(2.76, 3.24) * mm, "mid": v(2.35, 3.75) * mm, "end": v(1.93, 3.24) * mm});
            skLineSegment(sketch, "E186", {"start": v(1.93, 3.24) * mm, "end": v(2.12, 3.04) * mm});
            skLineSegment(sketch, "E187", {"start": v(2.12, 3.04) * mm, "end": v(2.58, 3.04) * mm});
            skLineSegment(sketch, "E188", {"start": v(2.58, 3.04) * mm, "end": v(2.76, 3.24) * mm});
            skLineSegment(sketch, "E189.MirrorCS", {"start": v(-2.58, 3.04) * mm, "end": v(-2.76, 3.24) * mm});
            skLineSegment(sketch, "E190.MirrorCS", {"start": v(-2.12, 3.04) * mm, "end": v(-2.58, 3.04) * mm});
            skArc(sketch, "E191.MirrorCS", {"start": v(-2.76, 3.24) * mm, "mid": v(-2.35, 3.75) * mm, "end": v(-1.93, 3.24) * mm});
            skLineSegment(sketch, "E192.MirrorCS", {"start": v(-1.93, 3.24) * mm, "end": v(-2.12, 3.04) * mm});
            skSolve(sketch);
        }
        {
            var Q0;
            Q0 = qSketchRegion(id + "F15", true);
            extrude(context, id + "F16", {"entities" : qUnion([Q0]), "operationType" : NewBodyOperationType.ADD, "depth" : 0.14 * mm});
        }
        {
            var Q0;
            Q0=makeQuery(id+"F12.boolean.opBoolean","COPY",FACE,{"derivedFrom":makeQuery(id+"F12.opExtrude","CAP_FACE",FACE,{"disambiguationData":[OSD([sQuery(id+"F11.wireOp",EDGE,"E162"),sQuery(id+"F11.wireOp",EDGE,"E163"),sQuery(id+"F11.wireOp",EDGE,"E164"),sQuery(id+"F11.wireOp",EDGE,"E165"),sQuery(id+"F11.wireOp",EDGE,"E166"),sQuery(id+"F11.wireOp",EDGE,"E167")])],"isStart":false})});
            var sketch = newSketch(context, id + "F17", { "sketchPlane" : qUnion([Q0])});
            skLineSegment(sketch, "E193", {"start": v(-2.67, -1.21) * mm, "end": v(-1.65, -0.87) * mm});
            skLineSegment(sketch, "E194", {"start": v(-1.65, -0.87) * mm, "end": v(-1.82, -3.89) * mm});
            skLineSegment(sketch, "E195", {"start": v(-1.82, -3.89) * mm, "end": v(-2.03, -3.87) * mm});
            skLineSegment(sketch, "E196", {"start": v(-2.03, -3.87) * mm, "end": v(-2.67, -1.21) * mm});
            skLineSegment(sketch, "E197", {"start": v(-0.94, -6.94) * mm, "end": v(-1.58, -7.18) * mm});
            skLineSegment(sketch, "E198", {"start": v(-1.58, -7.18) * mm, "end": v(-1.69, -4.59) * mm});
            skLineSegment(sketch, "E199", {"start": v(-1.69, -4.59) * mm, "end": v(-1.45, -4.58) * mm});
            skLineSegment(sketch, "E200", {"start": v(-1.45, -4.58) * mm, "end": v(-0.94, -6.94) * mm});
            skLineSegment(sketch, "E201.MirrorCS", {"start": v(1.69, -4.59) * mm, "end": v(1.45, -4.58) * mm});
            skLineSegment(sketch, "E202.MirrorCS", {"start": v(1.82, -3.89) * mm, "end": v(2.03, -3.87) * mm});
            skLineSegment(sketch, "E203.MirrorCS", {"start": v(1.58, -7.18) * mm, "end": v(1.69, -4.59) * mm});
            skLineSegment(sketch, "E204.MirrorCS", {"start": v(0.94, -6.94) * mm, "end": v(1.58, -7.18) * mm});
            skLineSegment(sketch, "E205.MirrorCS", {"start": v(2.03, -3.87) * mm, "end": v(2.67, -1.21) * mm});
            skLineSegment(sketch, "E206.MirrorCS", {"start": v(1.45, -4.58) * mm, "end": v(0.94, -6.94) * mm});
            skLineSegment(sketch, "E207.MirrorCS", {"start": v(1.65, -0.87) * mm, "end": v(1.82, -3.89) * mm});
            skLineSegment(sketch, "E208.MirrorCS", {"start": v(2.67, -1.21) * mm, "end": v(1.65, -0.87) * mm});
            skLineSegment(sketch, "E209", {"start": v(-0.16, -0.9) * mm, "end": v(-1.23, -0.9) * mm});
            skLineSegment(sketch, "E210", {"start": v(-1.23, -0.9) * mm, "end": v(-1.48, -1.92) * mm});
            skLineSegment(sketch, "E211", {"start": v(-1.48, -1.92) * mm, "end": v(-1.26, -1.92) * mm});
            skLineSegment(sketch, "E212", {"start": v(-1.26, -1.92) * mm, "end": v(-0.8, -1.28) * mm});
            skLineSegment(sketch, "E213", {"start": v(-0.8, -1.28) * mm, "end": v(-0.53, -1.64) * mm});
            skLineSegment(sketch, "E214", {"start": v(-0.53, -1.64) * mm, "end": v(-0.13, -1.33) * mm});
            skLineSegment(sketch, "E215.MirrorCS", {"start": v(1.48, -1.92) * mm, "end": v(1.26, -1.92) * mm});
            skLineSegment(sketch, "E216.MirrorCS", {"start": v(0.8, -1.28) * mm, "end": v(0.53, -1.64) * mm});
            skLineSegment(sketch, "E217.MirrorCS", {"start": v(0.16, -0.9) * mm, "end": v(1.23, -0.9) * mm});
            skLineSegment(sketch, "E218.MirrorCS", {"start": v(0.53, -1.64) * mm, "end": v(0.13, -1.33) * mm});
            skLineSegment(sketch, "E219.MirrorCS", {"start": v(1.26, -1.92) * mm, "end": v(0.8, -1.28) * mm});
            skLineSegment(sketch, "E220.MirrorCS", {"start": v(1.23, -0.9) * mm, "end": v(1.48, -1.92) * mm});
            skLineSegment(sketch, "E221", {"start": v(0.16, -0.9) * mm, "end": v(-0.16, -0.9) * mm});
            skLineSegment(sketch, "E222", {"start": v(-0.13, -1.33) * mm, "end": v(0.13, -1.33) * mm});
            skLineSegment(sketch, "E223", {"start": v(-0.67, -6.93) * mm, "end": v(-0.67, -6.12) * mm});
            skLineSegment(sketch, "E224", {"start": v(-0.67, -6.12) * mm, "end": v(-0.55, -6.12) * mm});
            skLineSegment(sketch, "E225", {"start": v(-0.55, -6.12) * mm, "end": v(-0.28, -6.64) * mm});
            skLineSegment(sketch, "E226", {"start": v(-0.67, -6.93) * mm, "end": v(-0.12, -6.93) * mm});
            skLineSegment(sketch, "E227.MirrorCS", {"start": v(0.67, -6.12) * mm, "end": v(0.55, -6.12) * mm});
            skLineSegment(sketch, "E228.MirrorCS", {"start": v(0.67, -6.93) * mm, "end": v(0.67, -6.12) * mm});
            skLineSegment(sketch, "E229.MirrorCS", {"start": v(0.67, -6.93) * mm, "end": v(0.12, -6.93) * mm});
            skLineSegment(sketch, "E230.MirrorCS", {"start": v(0.55, -6.12) * mm, "end": v(0.28, -6.64) * mm});
            skLineSegment(sketch, "E231", {"start": v(0.28, -6.64) * mm, "end": v(0, -6.27) * mm});
            skLineSegment(sketch, "E232", {"start": v(0, -6.27) * mm, "end": v(-0.28, -6.64) * mm});
            skLineSegment(sketch, "E233", {"start": v(-0.12, -6.93) * mm, "end": v(0.12, -6.93) * mm});
            skSolve(sketch);
        }
        {
            var Q0;
            Q0 = qSketchRegion(id + "F17", true);
            extrude(context, id + "F18", {"entities" : qUnion([Q0]), "operationType" : NewBodyOperationType.REMOVE, "oppositeDirection" : true, "depth" : 0.25 * mm});
        }
    });
